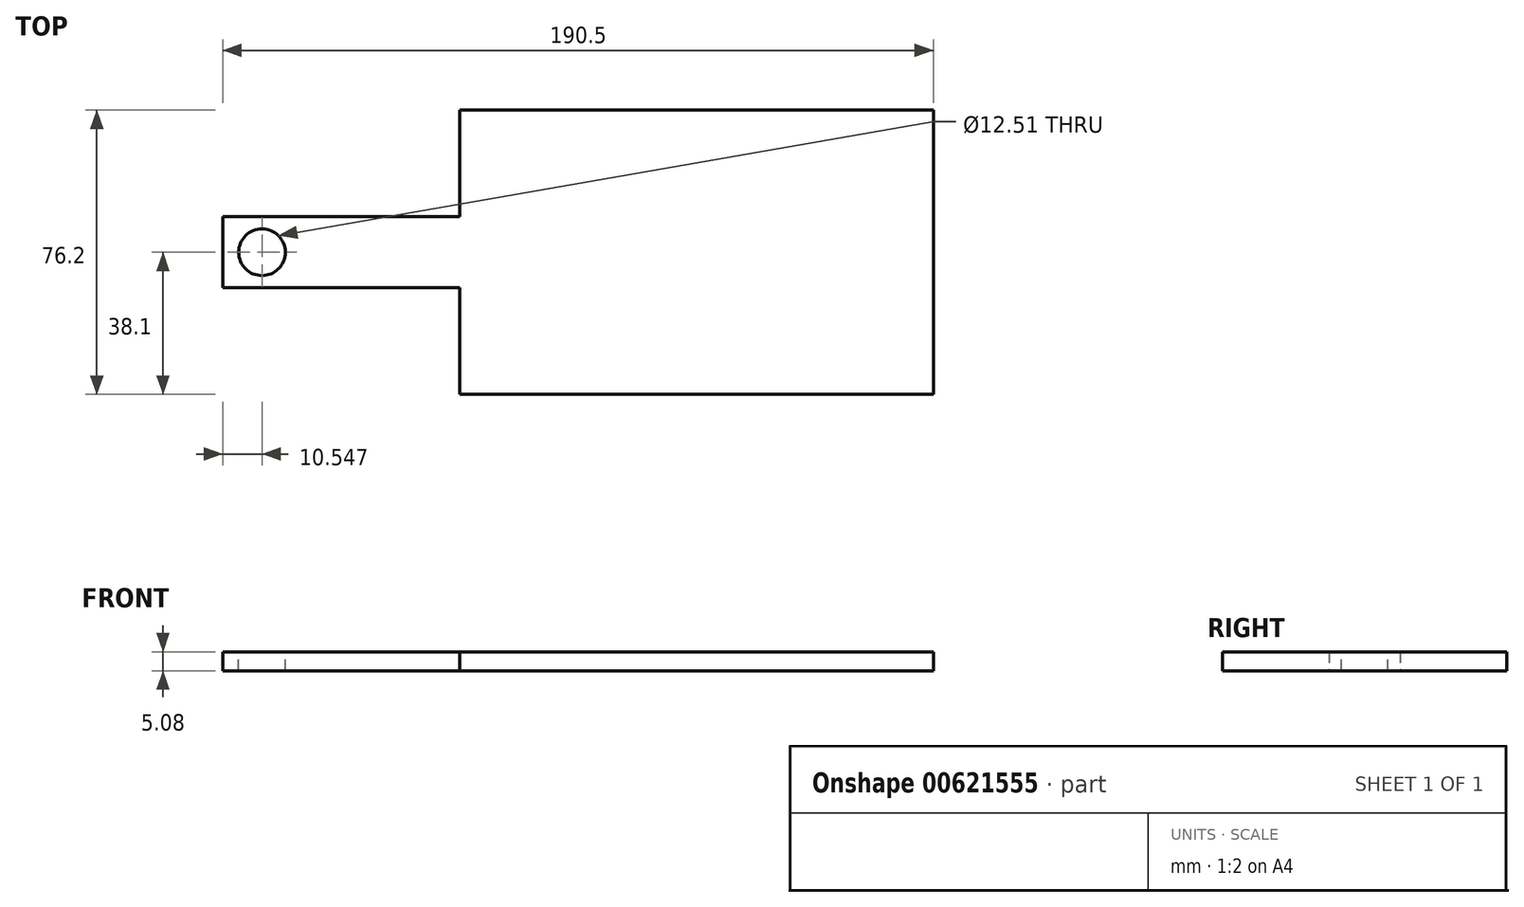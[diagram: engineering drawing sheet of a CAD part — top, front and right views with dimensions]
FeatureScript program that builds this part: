
annotation { "Feature Type Name" : "Feature", "Feature Type Description" : "" }
export const myFeature = defineFeature(function(context is Context, id is Id, definition is map)
    precondition{}
    {
        {
            var Q0;
            Q0=qCreatedBy(makeId("Top.planeOp"),FACE);
            var sketch = newSketch(context, id + "F0", { "sketchPlane" : qUnion([Q0])});
            skLineSegment(sketch, "E0.bottom", {"start": v(0, 0) * mm, "end": v(127, 0) * mm});
            skLineSegment(sketch, "E0.top", {"start": v(0, 76.2) * mm, "end": v(127, 76.2) * mm});
            skLineSegment(sketch, "E0.left", {"start": v(0, 0) * mm, "end": v(0, 76.2) * mm});
            skLineSegment(sketch, "E0.right", {"start": v(127, 0) * mm, "end": v(127, 76.2) * mm});
            skLineSegment(sketch, "E1.bottom", {"start": v(0, 47.63) * mm, "end": v(-63.5, 47.63) * mm});
            skLineSegment(sketch, "E1.top", {"start": v(0, 28.58) * mm, "end": v(-63.5, 28.58) * mm});
            skLineSegment(sketch, "E1.left", {"start": v(0, 47.63) * mm, "end": v(0, 28.58) * mm});
            skLineSegment(sketch, "E1.right", {"start": v(-63.5, 47.63) * mm, "end": v(-63.5, 28.58) * mm});
            skSolve(sketch);
        }
        {
            var Q0;
            {var subQ3=sQuery(id+"F0.wireOp",EDGE,"E0.bottom");Q0=makeQuery(id+"F0.imprint","IMPRINT",FACE,{"disambiguationData":[TD([[makeQuery(id+"F0.imprint","IMPRINT",EDGE,{"derivedFrom":subQ3}),1.0]])]});}
            var Q1;
            Q1=makeQuery(id+"F0.imprint","IMPRINT",FACE,{"disambiguationData":[TD([[makeQuery(id+"F0.imprint","IMPRINT",EDGE,{"derivedFrom":sQuery(id+"F0.wireOp",EDGE,"E1.bottom")}),1.0]])]});
            extrude(context, id + "F1", {"entities" : qUnion([Q0, Q1]), "depth" : 5.08 * mm, "offsetDistance" : 25.4 * mm});
        }
        {
            var Q0;
            Q0=makeQuery(id+"F1.opExtrude","CAP_FACE",FACE,{"disambiguationData":[OSD([sQuery(id+"F0.wireOp",EDGE,"E0.bottom"),sQuery(id+"F0.wireOp",EDGE,"E0.top"),sQuery(id+"F0.wireOp",EDGE,"E0.left"),sQuery(id+"F0.wireOp",EDGE,"E0.right"),sQuery(id+"F0.wireOp",EDGE,"E1.bottom"),sQuery(id+"F0.wireOp",EDGE,"E1.top"),sQuery(id+"F0.wireOp",EDGE,"E1.right")])],"isStart":false});
            var sketch = newSketch(context, id + "F2", { "sketchPlane" : qUnion([Q0])});
            skCircle(sketch, "E2", {"center": v(-52.95, 38.1) * mm, "radius": 6.25 * mm});
            skSolve(sketch);
        }
        {
            var Q0;
            Q0 = qSketchRegion(id + "F2", true);
            extrude(context, id + "F3", {"entities" : qUnion([Q0]), "operationType" : NewBodyOperationType.REMOVE, "oppositeDirection" : true, "depth" : 25.4 * mm, "offsetDistance" : 25.4 * mm});
        }
    });
